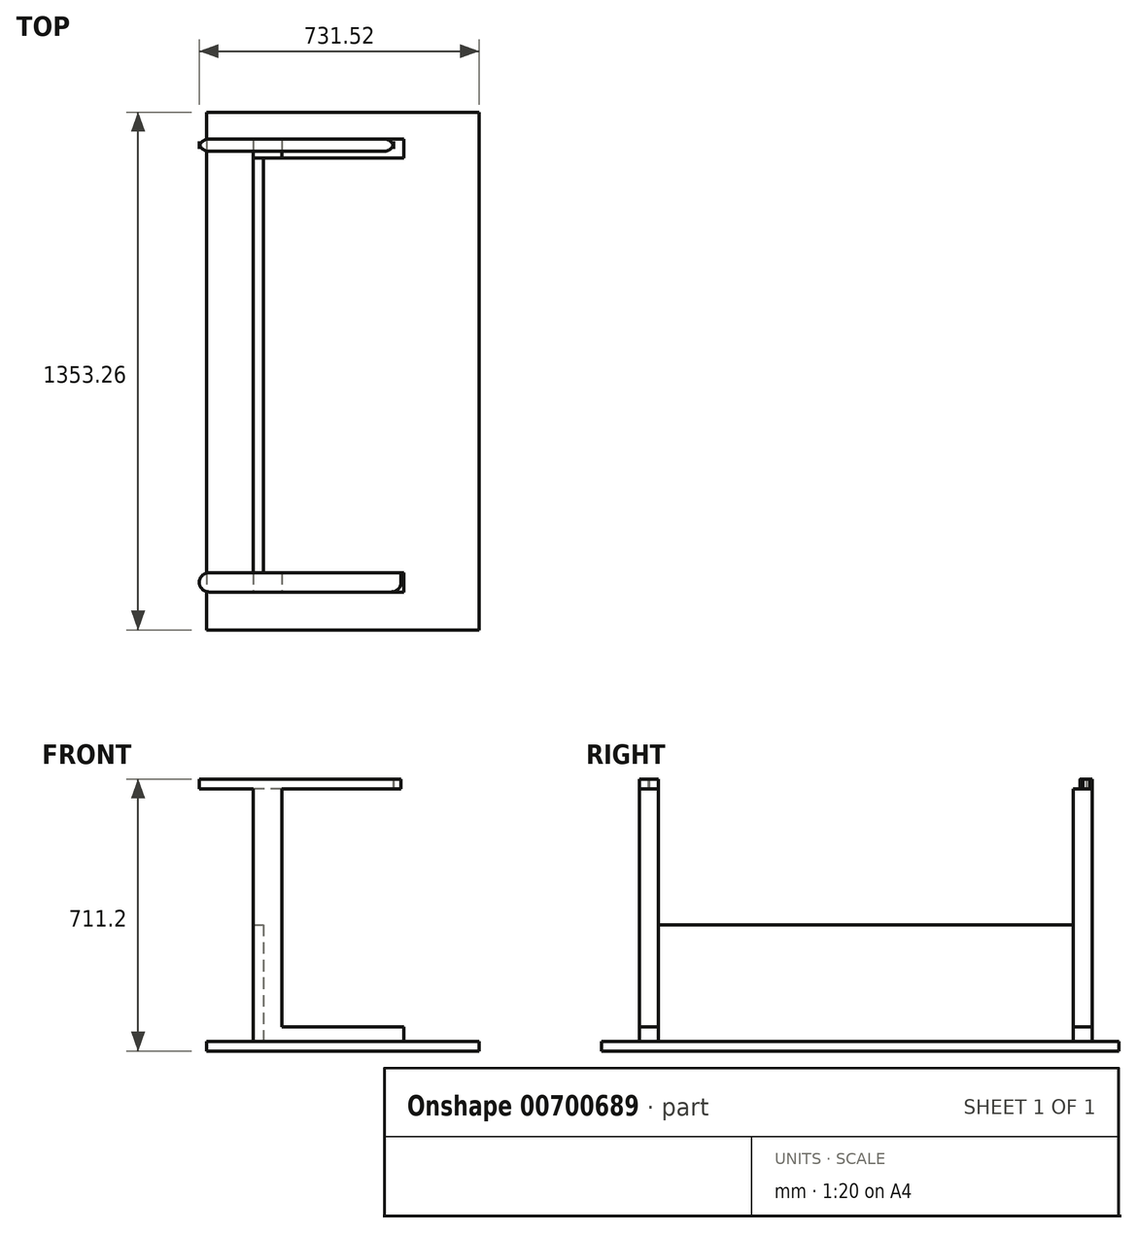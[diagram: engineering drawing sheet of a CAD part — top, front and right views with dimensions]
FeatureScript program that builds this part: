
annotation { "Feature Type Name" : "Feature", "Feature Type Description" : "" }
export const myFeature = defineFeature(function(context is Context, id is Id, definition is map)
    precondition{}
    {
        {
            var Q0;
            Q0=qCreatedBy(makeId("Top.planeOp"),FACE);
            var sketch = newSketch(context, id + "F0", { "sketchPlane" : qUnion([Q0])});
            skLineSegment(sketch, "E0.bottom", {"start": v(-356.02, 676.63) * mm, "end": v(356.02, 676.63) * mm});
            skLineSegment(sketch, "E0.top", {"start": v(-356.02, -676.63) * mm, "end": v(356.02, -676.63) * mm});
            skLineSegment(sketch, "E0.left", {"start": v(-356.02, 676.63) * mm, "end": v(-356.02, -676.63) * mm});
            skLineSegment(sketch, "E0.right", {"start": v(356.02, 676.63) * mm, "end": v(356.02, -676.63) * mm});
            skPoint(sketch, "E0.middle", {"position": v(0, 0) * mm});
            skSolve(sketch);
        }
        {
            var Q0;
            Q0=makeQuery(id+"F0.imprint","IMPRINT",FACE,{"disambiguationData":[TD([[makeQuery(id+"F0.imprint","IMPRINT",EDGE,{"derivedFrom":sQuery(id+"F0.wireOp",EDGE,"E0.bottom")}),-1.0]])]});
            extrude(context, id + "F1", {"entities" : qUnion([Q0]), "depth" : 25.4 * mm, "offsetDistance" : 25.4 * mm});
        }
        {
            var Q0;
            Q0=makeQuery(id+"F1.opExtrude","CAP_FACE",FACE,{"disambiguationData":[OSD([sQuery(id+"F0.wireOp",EDGE,"E0.bottom"),sQuery(id+"F0.wireOp",EDGE,"E0.top"),sQuery(id+"F0.wireOp",EDGE,"E0.left"),sQuery(id+"F0.wireOp",EDGE,"E0.right")])],"isStart":false});
            var sketch = newSketch(context, id + "F2", { "sketchPlane" : qUnion([Q0])});
            skLineSegment(sketch, "E1", {"start": v(356.02, 0) * mm, "end": v(-356.02, 0) * mm});
            skLineSegment(sketch, "E2.bottom", {"start": v(159.04, 606.88) * mm, "end": v(-159.04, 606.88) * mm});
            skLineSegment(sketch, "E2.top", {"start": v(159.04, 556.65) * mm, "end": v(-159.04, 556.65) * mm});
            skLineSegment(sketch, "E2.left", {"start": v(159.04, 606.88) * mm, "end": v(159.04, 556.65) * mm});
            skLineSegment(sketch, "E2.right", {"start": v(-159.04, 606.88) * mm, "end": v(-159.04, 556.65) * mm});
            skPoint(sketch, "E2.middle", {"position": v(0, 581.77) * mm});
            skSolve(sketch);
        }
        {
            var Q0;
            Q0=makeQuery(id+"F1.opExtrude","CAP_FACE",FACE,{"disambiguationData":[OSD([sQuery(id+"F0.wireOp",EDGE,"E0.bottom"),sQuery(id+"F0.wireOp",EDGE,"E0.top"),sQuery(id+"F0.wireOp",EDGE,"E0.left"),sQuery(id+"F0.wireOp",EDGE,"E0.right")])],"isStart":false});
            var sketch = newSketch(context, id + "F3", { "sketchPlane" : qUnion([Q0])});
            skLineSegment(sketch, "E3.bottom", {"start": v(-159.04, -527.36) * mm, "end": v(159.04, -527.36) * mm});
            skLineSegment(sketch, "E3.top", {"start": v(-159.04, -577.58) * mm, "end": v(159.04, -577.58) * mm});
            skLineSegment(sketch, "E3.left", {"start": v(-159.04, -527.36) * mm, "end": v(-159.04, -577.58) * mm});
            skLineSegment(sketch, "E3.right", {"start": v(159.04, -527.36) * mm, "end": v(159.04, -577.58) * mm});
            skPoint(sketch, "E3.middle", {"position": v(0, -552.47) * mm});
            skSolve(sketch);
        }
        {
            var Q0;
            Q0 = qSketchRegion(id + "F3", true);
            extrude(context, id + "F4", {"entities" : qUnion([Q0]), "operationType" : NewBodyOperationType.ADD, "depth" : 38.1 * mm, "offsetDistance" : 25.4 * mm});
        }
        {
            var Q0;
            Q0=makeQuery(id+"F2.imprint","IMPRINT",FACE,{"disambiguationData":[TD([[makeQuery(id+"F2.imprint","IMPRINT",EDGE,{"derivedFrom":sQuery(id+"F2.wireOp",EDGE,"E2.bottom")}),1.0]])]});
            extrude(context, id + "F5", {"entities" : qUnion([Q0]), "operationType" : NewBodyOperationType.ADD, "depth" : 38.1 * mm, "offsetDistance" : 25.4 * mm});
        }
        {
            var Q0;
            Q0=makeQuery(id+"F1.opExtrude","CAP_FACE",FACE,{"disambiguationData":[OSD([sQuery(id+"F0.wireOp",EDGE,"E0.bottom"),sQuery(id+"F0.wireOp",EDGE,"E0.top"),sQuery(id+"F0.wireOp",EDGE,"E0.left"),sQuery(id+"F0.wireOp",EDGE,"E0.right")])],"isStart":false});
            var sketch = newSketch(context, id + "F6", { "sketchPlane" : qUnion([Q0])});
            skLineSegment(sketch, "E4.bottom", {"start": v(-159.04, -527.36) * mm, "end": v(-234.38, -527.36) * mm});
            skLineSegment(sketch, "E4.top", {"start": v(-159.04, -577.58) * mm, "end": v(-234.38, -577.58) * mm});
            skLineSegment(sketch, "E4.left", {"start": v(-159.04, -527.36) * mm, "end": v(-159.04, -577.58) * mm});
            skLineSegment(sketch, "E4.right", {"start": v(-234.38, -527.36) * mm, "end": v(-234.38, -577.58) * mm});
            skLineSegment(sketch, "E5.bottom", {"start": v(-159.04, 606.88) * mm, "end": v(-234.38, 606.88) * mm});
            skLineSegment(sketch, "E5.top", {"start": v(-159.04, 556.65) * mm, "end": v(-234.38, 556.65) * mm});
            skLineSegment(sketch, "E5.left", {"start": v(-159.04, 606.88) * mm, "end": v(-159.04, 556.65) * mm});
            skLineSegment(sketch, "E5.right", {"start": v(-234.38, 606.88) * mm, "end": v(-234.38, 556.65) * mm});
            skSolve(sketch);
        }
        {
            var Q0;
            Q0 = qSketchRegion(id + "F6", true);
            extrude(context, id + "F7", {"entities" : qUnion([Q0]), "operationType" : NewBodyOperationType.ADD, "depth" : 660.4 * mm, "offsetDistance" : 25.4 * mm});
        }
        {
            var Q0;
            Q0=makeQuery(id+"F7.opExtrude","CAP_FACE",FACE,{"disambiguationData":[OSD([sQuery(id+"F6.wireOp",EDGE,"E4.bottom"),sQuery(id+"F6.wireOp",EDGE,"E4.top"),sQuery(id+"F6.wireOp",EDGE,"E4.left"),sQuery(id+"F6.wireOp",EDGE,"E4.right")])],"isStart":false});
            var sketch = newSketch(context, id + "F8", { "sketchPlane" : qUnion([Q0])});
            skLineSegment(sketch, "E6.bottom", {"start": v(-350.1, 606.88) * mm, "end": v(107.33, 606.88) * mm});
            skLineSegment(sketch, "E6.top", {"start": v(-350.1, 574.89) * mm, "end": v(107.33, 574.89) * mm});
            skLineSegment(sketch, "E6.left", {"start": v(-375.5, 600.29) * mm, "end": v(-375.5, 581.48) * mm});
            skLineSegment(sketch, "E6.right", {"start": v(132.73, 600.29) * mm, "end": v(132.73, 581.48) * mm});
            skLineSegment(sketch, "E7.bottom", {"start": v(-350.1, -527.36) * mm, "end": v(151.84, -527.36) * mm});
            skLineSegment(sketch, "E7.top", {"start": v(-350.1, -577.58) * mm, "end": v(126.44, -577.58) * mm});
            skLineSegment(sketch, "E7.left", {"start": v(-375.5, -552.18) * mm, "end": v(-375.5, -552.76) * mm});
            skLineSegment(sketch, "E7.right", {"start": v(151.84, -527.36) * mm, "end": v(151.84, -552.18) * mm});
            skPoint(sketch, "E8.visualSharp", {"position": v(132.73, 606.88) * mm});
            skArc(sketch, "E8.filletArc", {"start": v(132.73, 581.48) * mm, "mid": v(125.3, 599.44) * mm, "end": v(107.33, 606.88) * mm});
            skPoint(sketch, "E9.visualSharp", {"position": v(132.73, 574.89) * mm});
            skArc(sketch, "E9.filletArc", {"start": v(107.33, 574.89) * mm, "mid": v(125.3, 582.32) * mm, "end": v(132.73, 600.29) * mm});
            skPoint(sketch, "E10.visualSharp", {"position": v(-375.5, 606.88) * mm});
            skArc(sketch, "E10.filletArc", {"start": v(-350.1, 606.88) * mm, "mid": v(-368.06, 599.44) * mm, "end": v(-375.5, 581.48) * mm});
            skPoint(sketch, "E11.visualSharp", {"position": v(-375.5, 574.89) * mm});
            skArc(sketch, "E11.filletArc", {"start": v(-375.5, 600.29) * mm, "mid": v(-368.06, 582.32) * mm, "end": v(-350.1, 574.89) * mm});
            skPoint(sketch, "E12.visualSharp", {"position": v(-375.5, -527.36) * mm});
            skArc(sketch, "E12.filletArc", {"start": v(-350.1, -527.36) * mm, "mid": v(-368.06, -534.8) * mm, "end": v(-375.5, -552.76) * mm});
            skPoint(sketch, "E13.visualSharp", {"position": v(151.84, -577.58) * mm});
            skArc(sketch, "E13.filletArc", {"start": v(126.44, -577.58) * mm, "mid": v(144.4, -570.14) * mm, "end": v(151.84, -552.18) * mm});
            skPoint(sketch, "E14.visualSharp", {"position": v(-375.5, -577.58) * mm});
            skArc(sketch, "E14.filletArc", {"start": v(-375.5, -552.18) * mm, "mid": v(-368.06, -570.14) * mm, "end": v(-350.1, -577.58) * mm});
            skSolve(sketch);
        }
        {
            var Q0;
            Q0 = qSketchRegion(id + "F8", true);
            var Q1;
            Q1 = qSketchRegion(id + "F10", true);
            extrude(context, id + "F9", {"entities" : qUnion([Q0, Q1]), "operationType" : NewBodyOperationType.ADD, "depth" : 25.4 * mm, "offsetDistance" : 25.4 * mm});
        }
        {
            var Q0;
            Q0=makeQuery(id+"F1.opExtrude","CAP_FACE",FACE,{"disambiguationData":[OSD([sQuery(id+"F0.wireOp",EDGE,"E0.bottom"),sQuery(id+"F0.wireOp",EDGE,"E0.top"),sQuery(id+"F0.wireOp",EDGE,"E0.left"),sQuery(id+"F0.wireOp",EDGE,"E0.right")])],"isStart":false});
            var sketch = newSketch(context, id + "F10", { "sketchPlane" : qUnion([Q0])});
            skLineSegment(sketch, "E15.bottom", {"start": v(-234.38, -527.36) * mm, "end": v(-207.29, -527.36) * mm});
            skLineSegment(sketch, "E15.top", {"start": v(-234.38, 556.65) * mm, "end": v(-207.29, 556.65) * mm});
            skLineSegment(sketch, "E15.left", {"start": v(-234.38, -527.36) * mm, "end": v(-234.38, 556.65) * mm});
            skLineSegment(sketch, "E15.right", {"start": v(-207.29, -527.36) * mm, "end": v(-207.29, 556.65) * mm});
            skSolve(sketch);
        }
        {
            var Q0;
            Q0 = qSketchRegion(id + "F10", true);
            extrude(context, id + "F11", {"entities" : qUnion([Q0]), "operationType" : NewBodyOperationType.ADD, "depth" : 304.8 * mm, "offsetDistance" : 25.4 * mm});
        }
    });
